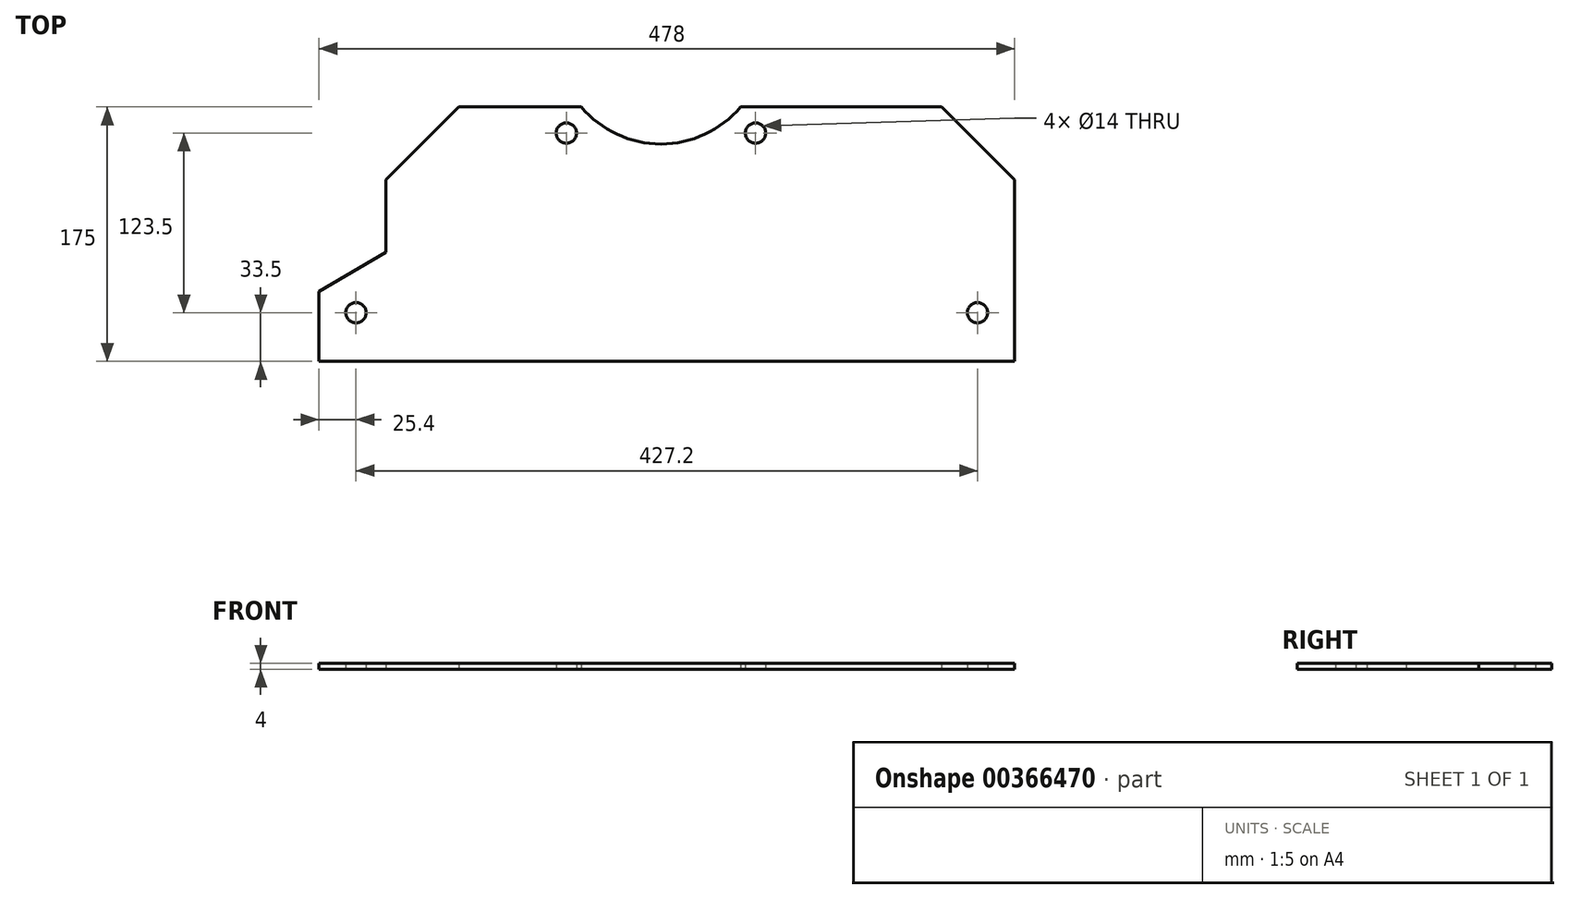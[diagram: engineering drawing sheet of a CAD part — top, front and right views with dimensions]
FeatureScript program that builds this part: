
annotation { "Feature Type Name" : "Feature", "Feature Type Description" : "" }
export const myFeature = defineFeature(function(context is Context, id is Id, definition is map)
    precondition{}
    {
        {
            var Q0;
            Q0=qCreatedBy(makeId("Top.planeOp"),FACE);
            var sketch = newSketch(context, id + "F0", { "sketchPlane" : qUnion([Q0])});
            skLineSegment(sketch, "E0.bottom", {"start": v(-143, 87.5) * mm, "end": v(-58.74, 87.5) * mm});
            skLineSegment(sketch, "E0.top", {"start": v(-239, -87.5) * mm, "end": v(239, -87.5) * mm});
            skLineSegment(sketch, "E0.left", {"start": v(-239, -39.5) * mm, "end": v(-239, -87.5) * mm});
            skLineSegment(sketch, "E0.right", {"start": v(239, 37.5) * mm, "end": v(239, -87.5) * mm});
            skLineSegment(sketch, "E1", {"start": v(-305.05, -12.5) * mm, "end": v(-239, -12.5) * mm, "construction": true});
            skCircle(sketch, "E2", {"center": v(-213.6, -54) * mm, "radius": 7 * mm});
            skCircle(sketch, "E3", {"center": v(213.6, -54) * mm, "radius": 7 * mm});
            skLineSegment(sketch, "E4", {"start": v(-193, -12.5) * mm, "end": v(-239, -39.5) * mm});
            skLineSegment(sketch, "E5", {"start": v(-193, 37.5) * mm, "end": v(-193, -12.5) * mm});
            skLineSegment(sketch, "E6.trimOffspring", {"start": v(-193, -12.5) * mm, "end": v(361.51, -12.5) * mm, "construction": true});
            skLineSegment(sketch, "E7", {"start": v(-143, 87.5) * mm, "end": v(-193, 37.5) * mm});
            skPoint(sketch, "E8.orphan", {"position": v(-193, 87.5) * mm});
            skArc(sketch, "E9", {"start": v(-58.74, 87.5) * mm, "mid": v(-4, 62) * mm, "end": v(50.74, 87.5) * mm});
            skLineSegment(sketch, "E10.trimOffspring", {"start": v(50.74, 87.5) * mm, "end": v(189, 87.5) * mm});
            skCircle(sketch, "E11", {"center": v(-69, 69.5) * mm, "radius": 7 * mm});
            skCircle(sketch, "E12", {"center": v(61, 69.5) * mm, "radius": 7 * mm});
            skLineSegment(sketch, "E13", {"start": v(189, 87.5) * mm, "end": v(239, 37.5) * mm});
            skPoint(sketch, "E14.orphan", {"position": v(239, 87.5) * mm});
            skSolve(sketch);
        }
        {
            var Q0;
            Q0=makeQuery(id+"F0.imprint","IMPRINT",FACE,{"disambiguationData":[TD([[makeQuery(id+"F0.imprint","IMPRINT",EDGE,{"derivedFrom":sQuery(id+"F0.wireOp",EDGE,"E0.bottom")}),-1.0]])]});
            extrude(context, id + "F1", {"entities" : qUnion([Q0]), "endBound" : BoundingType.SYMMETRIC, "depth" : 4 * mm});
        }
    });
